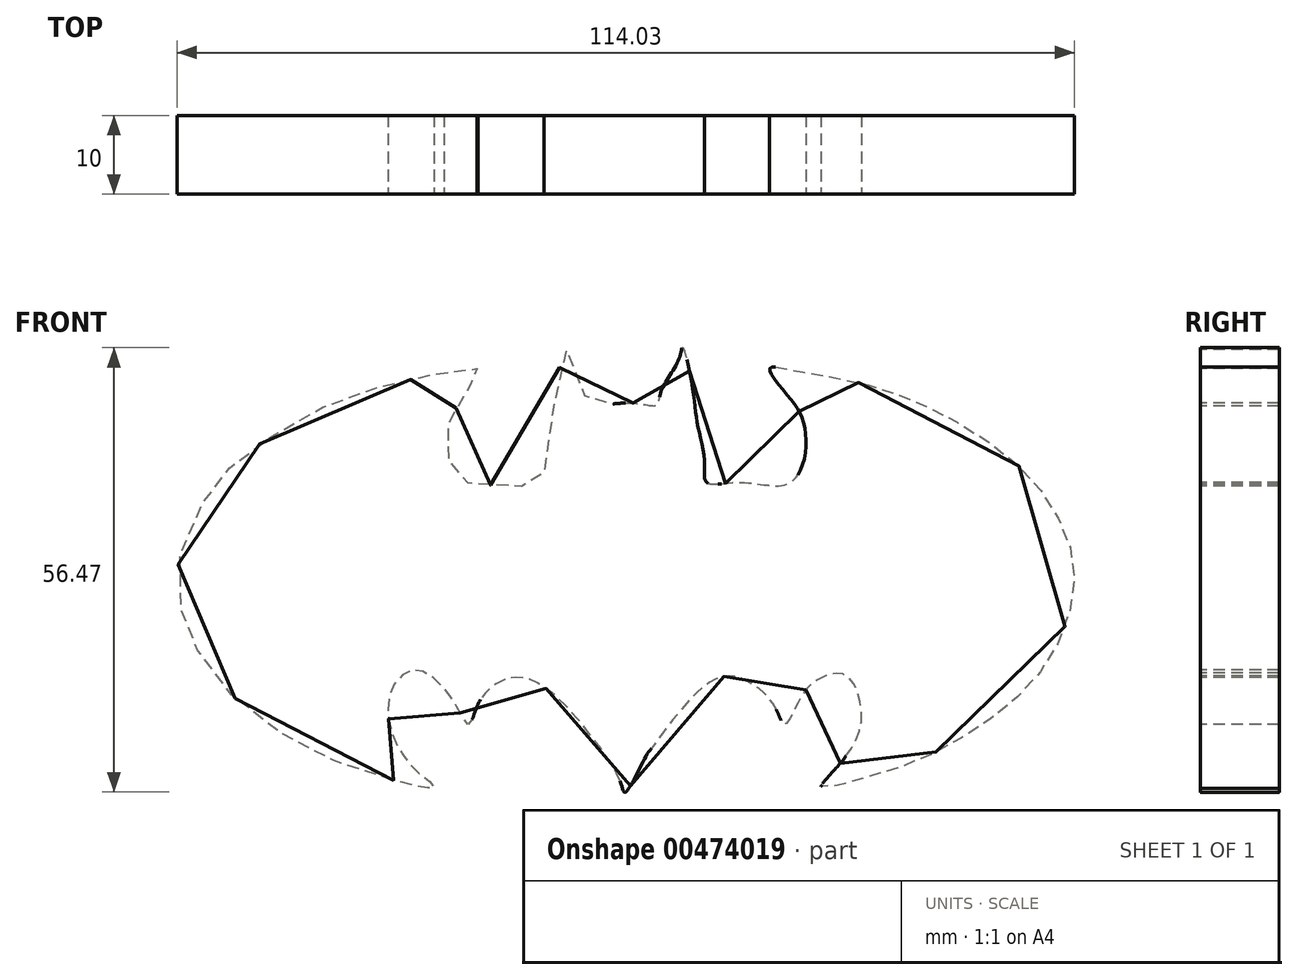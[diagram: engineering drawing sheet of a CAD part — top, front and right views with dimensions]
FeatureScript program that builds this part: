
annotation { "Feature Type Name" : "Feature", "Feature Type Description" : "" }
export const myFeature = defineFeature(function(context is Context, id is Id, definition is map)
    precondition{}
    {
        {
            var Q0;
            Q0=qCreatedBy(makeId("Front.planeOp"),FACE);
            var sketch = newSketch(context, id + "F0", { "sketchPlane" : qUnion([Q0])});
            skFitSpline(sketch, "E0", {"points": [v(-30.44, -25.8) * mm, v(-38.46, -23.1) * mm, v(-45.13, -19.55) * mm, v(-51.52, -14.37) * mm, v(-55.36, -9.18) * mm, v(-56.95, -5.56) * mm, v(-57.92, 0) * mm, v(-56.1, 6.82) * mm, v(-53.19, 11.56) * mm, v(-50.64, 14.47) * mm, v(-45.54, 18.12) * mm, v(-38.98, 21.76) * mm, v(-33.03, 23.95) * mm, v(-25.99, 25.65) * mm, v(-19.67, 26.62) * mm, v(-19.8, 26.5) * mm, v(-19.8, 26.62) * mm, v(-19.67, 25.65) * mm, v(-20.16, 25.04) * mm, v(-22.34, 21.76) * mm, v(-23.92, 18.12) * mm, v(-23.68, 15.32) * mm, v(-22.34, 13.02) * mm, v(-21.5, 12.17) * mm, v(-17.24, 11.68) * mm, v(-11.41, 11.92) * mm, v(-11.3, 12.53) * mm, v(-10.44, 18.48) * mm, v(-8.62, 28.92) * mm, v(-7.65, 26.98) * mm, v(-5.7, 22.12) * mm, v(-5.22, 21.76) * mm, v(0, 22.12) * mm, v(3.03, 21.88) * mm, v(3.52, 23.46) * mm, v(5.83, 27.7) * mm, v(6.31, 29.17) * mm, v(7.53, 24.19) * mm, v(8.26, 19.2) * mm, v(9.1, 14.47) * mm, v(9.35, 12.05) * mm, v(13.72, 12.05) * mm, v(19.55, 11.8) * mm, v(21.73, 14.96) * mm, v(21.61, 19.82) * mm, v(19.55, 23.22) * mm, v(17.36, 26.5) * mm, v(19.91, 26.37) * mm, v(27.8, 24.92) * mm, v(34.6, 22.85) * mm, v(41.77, 19.33) * mm, v(49.66, 13.5) * mm, v(54.4, 6.7) * mm, v(56.1, 0) * mm, v(54.16, -8) * mm, v(49.42, -14.67) * mm, v(42.38, -20.01) * mm, v(35.21, -23.65) * mm, v(27.32, -26.08) * mm, v(23.92, -26.69) * mm, v(26.1, -23.9) * mm, v(29.02, -18.07) * mm, v(27.08, -12.48) * mm, v(24.04, -12.73) * mm, v(21.37, -15.15) * mm, v(19.3, -18.68) * mm, v(18.1, -16.61) * mm, v(15.18, -13.58) * mm, v(11.53, -12.6) * mm, v(6.92, -15.88) * mm, v(2.91, -20.98) * mm, v(1.33, -23.29) * mm, v(-0.97, -27.3) * mm, v(-1.7, -25.72) * mm, v(-5.34, -20.13) * mm, v(-9.23, -15.64) * mm, v(-13.6, -12.85) * mm, v(-17, -13.33) * mm, v(-19.67, -16.13) * mm, v(-20.89, -18.68) * mm, v(-22.34, -16.5) * mm, v(-24.77, -13.33) * mm, v(-27.8, -11.75) * mm, v(-30.6, -14.06) * mm, v(-30.96, -18.43) * mm, v(-29.63, -21.95) * mm, v(-27.2, -24.87) * mm, v(-25.26, -26.69) * mm, v(-30.44, -25.8) * mm]});
            skSolve(sketch);
        }
        {
            var Q0;
            Q0=makeQuery(id+"F0.imprint","IMPRINT",FACE,{"disambiguationData":[TD([[makeQuery(id+"F0.imprint","IMPRINT",EDGE,{"derivedFrom":sQuery(id+"F0.wireOp",EDGE,"E0")}),-1.0]])]});
            extrude(context, id + "F1", {"entities" : qUnion([Q0]), "oppositeDirection" : true, "depth" : 10 * mm});
        }
    });
